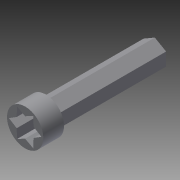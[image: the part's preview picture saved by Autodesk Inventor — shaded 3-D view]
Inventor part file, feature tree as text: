
AUTODESK INVENTOR PART (.ipt)
format: ipt  version: 2015 (Build 190159000, 159)  size: 123,904 bytes
history: native  units: in
note: dims shown in document units (in); Inventor stores cm internally (conversion verified against a paired STEP export)
features: extrude x4, sketch x4, projected_geometry x1
ambient origin geometry x8: Origin, YZ Plane, XZ Plane, XY Plane, X Axis, Y Axis, Z Axis, Center Point
bodies: Solid1 (feature_tree)
feature tree (9):
  extrude  "Extrusion1"  Depth=0.1083in
  extrude  "Extrusion2"  Depth=1.25in
  extrude  "Extrusion3"  Depth=0.2in
  extrude  "Extrusion4"  Depth=0.175in
  sketch  "Sketch1"  dims[d0=0.25in d1=0.1083in]
  sketch  "Sketch2"  dims[d2=1.25in d3=0.0in d4=0.35in]
  sketch  "Sketch3"  dims[d5=0.2in d6=0.0in d7=0.313in]
  sketch  "Sketch4"  dims[d8=0.1875in d9=0.0796in d10=60.0deg d11=0.0938in d12=2.3622in d14=360.0deg d16=0.175in d17=0.0in d18=0.175in d19=0.0in]
  projected_geometry  "Projected Loop1"
